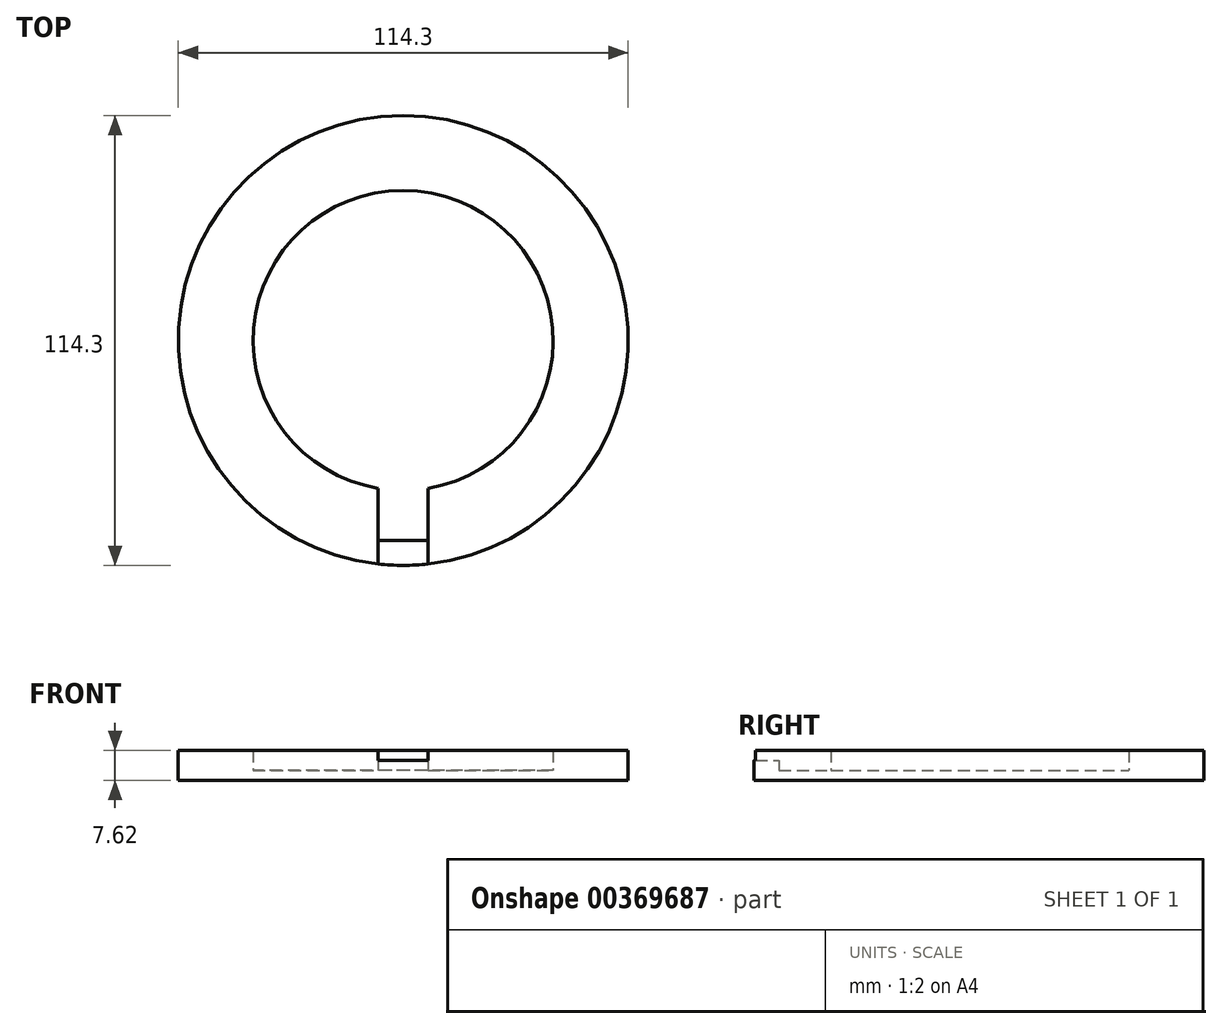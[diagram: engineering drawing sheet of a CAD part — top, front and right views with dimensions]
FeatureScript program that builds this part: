
annotation { "Feature Type Name" : "Feature", "Feature Type Description" : "" }
export const myFeature = defineFeature(function(context is Context, id is Id, definition is map)
    precondition{}
    {
        {
            assignVariable(context, id + "F0", {"name" : "t", "anyValue" : 2.54 * mm});
        }
        {
            var Q0;
            Q0=qCreatedBy(makeId("Top.planeOp"),FACE);
            var sketch = newSketch(context, id + "F1", { "sketchPlane" : qUnion([Q0])});
            skCircle(sketch, "E0", {"center": v(0, 0) * mm, "radius": 57.15 * mm});
            skSolve(sketch);
        }
        {
            var Q0;
            Q0=makeQuery(id+"F1.imprint","IMPRINT",FACE,{"disambiguationData":[TD([[makeQuery(id+"F1.imprint","IMPRINT",EDGE,{"derivedFrom":sQuery(id+"F1.wireOp",EDGE,"E0")}),1.0]])]});
            var Q1;
            Q1=sQuery(id+"F1.wireOp",EDGE,"E0");
            extrude(context, id + "F2", {"entities" : qUnion([Q0]), "surfaceEntities" : qUnion([Q1]), "depth" : getVariable(context, 't')});
        }
        {
            var Q0;
            Q0=makeQuery(id+"F2.opExtrude","CAP_FACE",FACE,{"disambiguationData":[OSD([sQuery(id+"F1.wireOp",EDGE,"E0")])],"isStart":false});
            var sketch = newSketch(context, id + "F3", { "sketchPlane" : qUnion([Q0])});
            skCircle(sketch, "E1", {"center": v(0, 0) * mm, "radius": 57.15 * mm});
            skArc(sketch, "E2", {"start": v(6.35, -37.57) * mm, "mid": v(0, 38.1) * mm, "end": v(-6.35, -37.57) * mm});
            skLineSegment(sketch, "E3.bottom", {"start": v(6.35, -50.8) * mm, "end": v(-6.35, -50.8) * mm});
            skLineSegment(sketch, "E3.left", {"start": v(6.35, -50.8) * mm, "end": v(6.35, -37.57) * mm});
            skLineSegment(sketch, "E3.right", {"start": v(-6.35, -50.8) * mm, "end": v(-6.35, -37.57) * mm});
            skPoint(sketch, "E3.middle", {"position": v(0, -38.1) * mm});
            skPoint(sketch, "E4.orphan", {"position": v(6.35, -25.4) * mm});
            skPoint(sketch, "E5.orphan", {"position": v(-6.35, -25.4) * mm});
            skSolve(sketch);
        }
        {
            var Q0;
            Q0=makeQuery(id+"F3.imprint","IMPRINT",FACE,{"disambiguationData":[TD([[makeQuery(id+"F3.imprint","IMPRINT",EDGE,{"derivedFrom":sQuery(id+"F3.wireOp",EDGE,"E1")}),1.0]])]});
            extrude(context, id + "F4", {"entities" : qUnion([Q0]), "operationType" : NewBodyOperationType.ADD, "depth" : getVariable(context, 't')});
        }
        {
            var Q0;
            Q0=makeQuery(id+"F4.opExtrude","CAP_FACE",FACE,{"disambiguationData":[OSD([sQuery(id+"F3.wireOp",EDGE,"E1"),sQuery(id+"F3.wireOp",EDGE,"E2"),sQuery(id+"F3.wireOp",EDGE,"E3.bottom"),sQuery(id+"F3.wireOp",EDGE,"E3.left"),sQuery(id+"F3.wireOp",EDGE,"E3.right")])],"isStart":false});
            var sketch = newSketch(context, id + "F5", { "sketchPlane" : qUnion([Q0])});
            skArc(sketch, "E6", {"start": v(6.35, -56.8) * mm, "mid": v(0, 57.15) * mm, "end": v(-6.35, -56.8) * mm});
            skArc(sketch, "E7", {"start": v(6.35, -37.57) * mm, "mid": v(0, 38.1) * mm, "end": v(-6.35, -37.57) * mm});
            skLineSegment(sketch, "E8.left", {"start": v(6.35, -37.57) * mm, "end": v(6.35, -56.8) * mm});
            skLineSegment(sketch, "E8.right", {"start": v(-6.35, -37.57) * mm, "end": v(-6.35, -56.8) * mm});
            skPoint(sketch, "E8.middle", {"position": v(0, -38.1) * mm});
            skPoint(sketch, "E9.orphan", {"position": v(-6.35, -12.7) * mm});
            skPoint(sketch, "E10.orphan", {"position": v(6.35, -12.7) * mm});
            skPoint(sketch, "E11.orphan", {"position": v(-6.35, -63.5) * mm});
            skPoint(sketch, "E12.orphan", {"position": v(6.35, -63.5) * mm});
            skSolve(sketch);
        }
        {
            var Q0;
            {var subQ0=sQuery(id+"F5.wireOp",EDGE,"E8.left");var subQ5=sQuery(id+"F5.wireOp",EDGE,"E6");var subQ6=makeQuery(id+"F5.imprint","INTERSECT",VERTEX,{"derivedFrom":[subQ5,subQ0]});Q0=makeQuery(id+"F5.imprint","IMPRINT",FACE,{"disambiguationData":[TD([[makeQuery(id+"F5.imprint","IMPRINT",EDGE,{"disambiguationData":[TD([[subQ6,-1.0]])],"derivedFrom":subQ5}),1.0]])]});}
            extrude(context, id + "F6", {"entities" : qUnion([Q0]), "operationType" : NewBodyOperationType.ADD, "depth" : getVariable(context, 't')});
        }
    });
